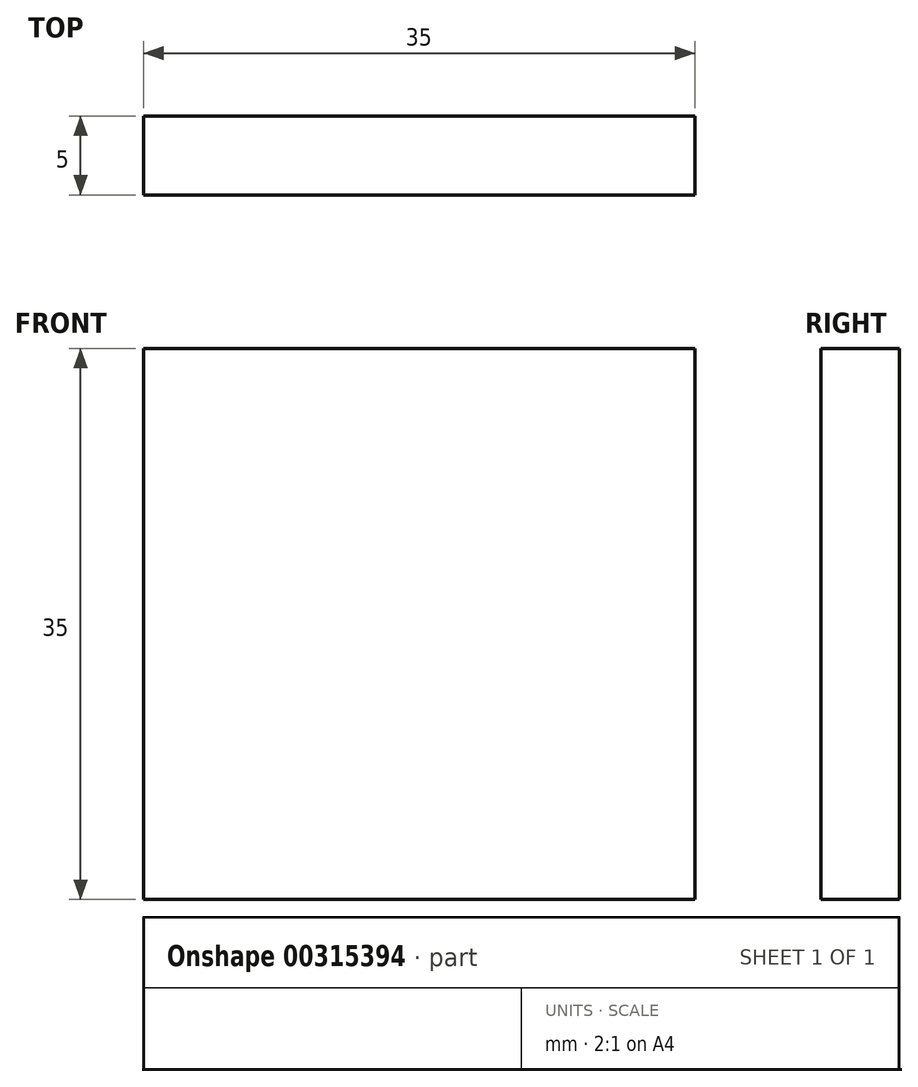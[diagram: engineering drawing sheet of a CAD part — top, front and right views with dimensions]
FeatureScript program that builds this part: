
annotation { "Feature Type Name" : "Feature", "Feature Type Description" : "" }
export const myFeature = defineFeature(function(context is Context, id is Id, definition is map)
    precondition{}
    {
        {
            var Q0;
            Q0=qCreatedBy(makeId("Front.planeOp"),FACE);
            var sketch = newSketch(context, id + "F0", { "sketchPlane" : qUnion([Q0])});
            skLineSegment(sketch, "E0.bottom", {"start": v(-17.5, 17.5) * mm, "end": v(17.5, 17.5) * mm});
            skLineSegment(sketch, "E0.top", {"start": v(-17.5, -17.5) * mm, "end": v(17.5, -17.5) * mm});
            skLineSegment(sketch, "E0.left", {"start": v(-17.5, 17.5) * mm, "end": v(-17.5, -17.5) * mm});
            skLineSegment(sketch, "E0.right", {"start": v(17.5, 17.5) * mm, "end": v(17.5, -17.5) * mm});
            skPoint(sketch, "E0.middle", {"position": v(0, 0) * mm});
            skSolve(sketch);
        }
        {
            var Q0;
            Q0=makeQuery(id+"F0.imprint","IMPRINT",FACE,{"disambiguationData":[TD([[makeQuery(id+"F0.imprint","IMPRINT",EDGE,{"derivedFrom":sQuery(id+"F0.wireOp",EDGE,"E0.bottom")}),-1.0]])]});
            extrude(context, id + "F1", {"entities" : qUnion([Q0]), "depth" : 5 * mm});
        }
    });
